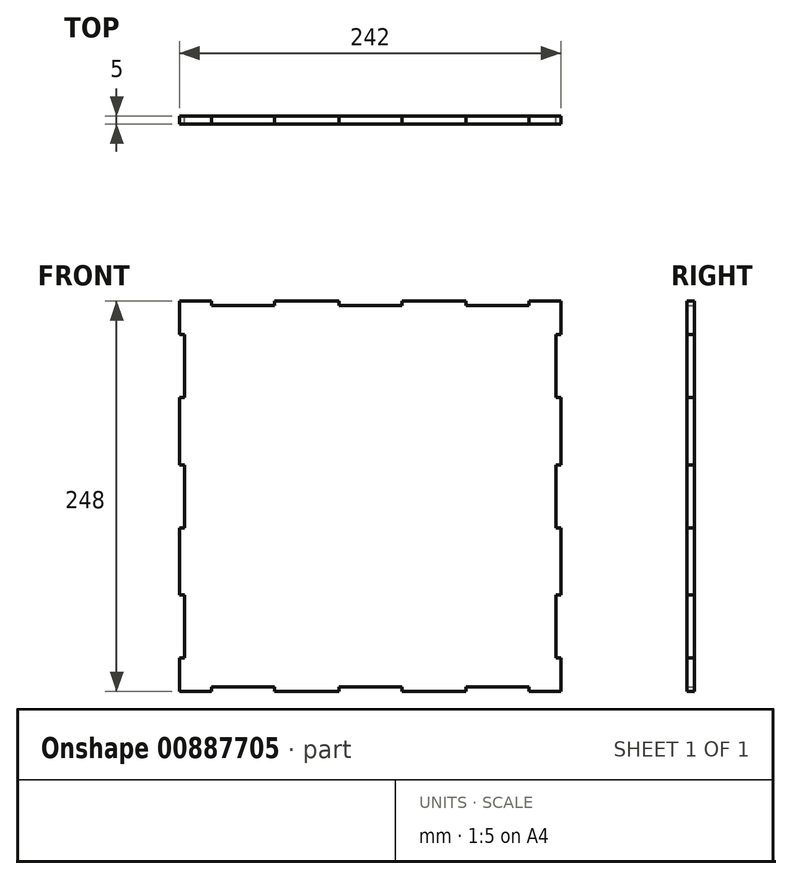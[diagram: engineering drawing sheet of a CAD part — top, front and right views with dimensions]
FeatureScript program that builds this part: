
annotation { "Feature Type Name" : "Feature", "Feature Type Description" : "" }
export const myFeature = defineFeature(function(context is Context, id is Id, definition is map)
    precondition{}
    {
        {
            var Q0;
            Q0=qCreatedBy(makeId("Front.planeOp"),FACE);
            var sketch = newSketch(context, id + "F0", { "sketchPlane" : qUnion([Q0])});
            skLineSegment(sketch, "E0.bottom", {"start": v(121, -124) * mm, "end": v(100.7, -124) * mm});
            skLineSegment(sketch, "E0.top", {"start": v(121, 124) * mm, "end": v(100.7, 124) * mm});
            skLineSegment(sketch, "E0.left", {"start": v(121, -124) * mm, "end": v(121, -102.67) * mm});
            skLineSegment(sketch, "E0.right", {"start": v(-121, -124) * mm, "end": v(-121, -102.67) * mm});
            skPoint(sketch, "E0.middle", {"position": v(0, 0) * mm});
            skLineSegment(sketch, "E1", {"start": v(-121, 102.67) * mm, "end": v(-118, 102.67) * mm});
            skLineSegment(sketch, "E2", {"start": v(-118, 102.67) * mm, "end": v(-118, 62.67) * mm});
            skLineSegment(sketch, "E3", {"start": v(-118, 62.67) * mm, "end": v(-121, 62.67) * mm});
            skLineSegment(sketch, "E4", {"start": v(-121, 20) * mm, "end": v(-118, 20) * mm});
            skLineSegment(sketch, "E5", {"start": v(-118, 20) * mm, "end": v(-118, -20) * mm});
            skLineSegment(sketch, "E6", {"start": v(-118, -20) * mm, "end": v(-121, -20) * mm});
            skLineSegment(sketch, "E7.MirrorCS", {"start": v(-118, -102.67) * mm, "end": v(-118, -62.67) * mm});
            skLineSegment(sketch, "E8.MirrorCS", {"start": v(-118, -62.67) * mm, "end": v(-121, -62.67) * mm});
            skLineSegment(sketch, "E9.MirrorCS", {"start": v(-121, -102.67) * mm, "end": v(-118, -102.67) * mm});
            skLineSegment(sketch, "E10.MirrorCS", {"start": v(118, 102.67) * mm, "end": v(118, 62.67) * mm});
            skLineSegment(sketch, "E11.MirrorCS", {"start": v(121, 102.67) * mm, "end": v(118, 102.67) * mm});
            skLineSegment(sketch, "E12.MirrorCS", {"start": v(118, 62.67) * mm, "end": v(121, 62.67) * mm});
            skLineSegment(sketch, "E13.MirrorCS", {"start": v(121, 20) * mm, "end": v(118, 20) * mm});
            skLineSegment(sketch, "E14.MirrorCS", {"start": v(118, 20) * mm, "end": v(118, -20) * mm});
            skLineSegment(sketch, "E15.MirrorCS", {"start": v(118, -20) * mm, "end": v(121, -20) * mm});
            skLineSegment(sketch, "E16.MirrorCS", {"start": v(118, -102.67) * mm, "end": v(118, -62.67) * mm});
            skLineSegment(sketch, "E17.MirrorCS", {"start": v(118, -62.67) * mm, "end": v(121, -62.67) * mm});
            skLineSegment(sketch, "E18.MirrorCS", {"start": v(121, -102.67) * mm, "end": v(118, -102.67) * mm});
            skLineSegment(sketch, "E19.trimOffspring", {"start": v(-121, 102.67) * mm, "end": v(-121, 124) * mm});
            skLineSegment(sketch, "E20.trimOffspring", {"start": v(-121, 20) * mm, "end": v(-121, 62.67) * mm});
            skLineSegment(sketch, "E21.trimOffspring", {"start": v(-121, -62.67) * mm, "end": v(-121, -20) * mm});
            skLineSegment(sketch, "E22.trimOffspring", {"start": v(121, 102.67) * mm, "end": v(121, 124) * mm});
            skLineSegment(sketch, "E23.trimOffspring", {"start": v(121, 20) * mm, "end": v(121, 62.67) * mm});
            skLineSegment(sketch, "E24.trimOffspring", {"start": v(121, -62.67) * mm, "end": v(121, -20) * mm});
            skLineSegment(sketch, "E25", {"start": v(100.7, -124) * mm, "end": v(100.7, -121) * mm});
            skLineSegment(sketch, "E26", {"start": v(100.7, -121) * mm, "end": v(60.7, -121) * mm});
            skLineSegment(sketch, "E27", {"start": v(60.7, -121) * mm, "end": v(60.7, -124) * mm});
            skLineSegment(sketch, "E28", {"start": v(20, -124) * mm, "end": v(20, -121) * mm});
            skLineSegment(sketch, "E29", {"start": v(20, -121) * mm, "end": v(-20, -121) * mm});
            skLineSegment(sketch, "E30", {"start": v(-20, -121) * mm, "end": v(-20, -124) * mm});
            skLineSegment(sketch, "E31.MirrorCS", {"start": v(-100.7, -124) * mm, "end": v(-100.7, -121) * mm});
            skLineSegment(sketch, "E32.MirrorCS", {"start": v(-100.7, -121) * mm, "end": v(-60.7, -121) * mm});
            skLineSegment(sketch, "E33.MirrorCS", {"start": v(-60.7, -121) * mm, "end": v(-60.7, -124) * mm});
            skLineSegment(sketch, "E34.trimOffspring", {"start": v(60.7, -124) * mm, "end": v(20, -124) * mm});
            skLineSegment(sketch, "E35.trimOffspring", {"start": v(-20, -124) * mm, "end": v(-60.7, -124) * mm});
            skLineSegment(sketch, "E36.trimOffspring", {"start": v(-100.7, -124) * mm, "end": v(-121, -124) * mm});
            skLineSegment(sketch, "E37.MirrorCS", {"start": v(100.7, 121) * mm, "end": v(60.7, 121) * mm});
            skLineSegment(sketch, "E38.MirrorCS", {"start": v(100.7, 124) * mm, "end": v(100.7, 121) * mm});
            skLineSegment(sketch, "E39.MirrorCS", {"start": v(60.7, 121) * mm, "end": v(60.7, 124) * mm});
            skLineSegment(sketch, "E40.MirrorCS", {"start": v(20, 124) * mm, "end": v(20, 121) * mm});
            skLineSegment(sketch, "E41.MirrorCS", {"start": v(20, 121) * mm, "end": v(-20, 121) * mm});
            skLineSegment(sketch, "E42.MirrorCS", {"start": v(-20, 121) * mm, "end": v(-20, 124) * mm});
            skLineSegment(sketch, "E43.MirrorCS", {"start": v(-60.7, 121) * mm, "end": v(-60.7, 124) * mm});
            skLineSegment(sketch, "E44.MirrorCS", {"start": v(-100.7, 121) * mm, "end": v(-60.7, 121) * mm});
            skLineSegment(sketch, "E45.MirrorCS", {"start": v(-100.7, 124) * mm, "end": v(-100.7, 121) * mm});
            skLineSegment(sketch, "E46.trimOffspring", {"start": v(-20, 124) * mm, "end": v(-60.7, 124) * mm});
            skLineSegment(sketch, "E47.trimOffspring", {"start": v(-100.7, 124) * mm, "end": v(-121, 124) * mm});
            skLineSegment(sketch, "E48.trimOffspring", {"start": v(60.7, 124) * mm, "end": v(20, 124) * mm});
            skSolve(sketch);
        }
        {
            var Q0;
            Q0 = qSketchRegion(id + "F0", true);
            var Q1;
            Q1=makeQuery(id+"F0.imprint","IMPRINT",FACE,{"disambiguationData":[TD([[makeQuery(id+"F0.imprint","IMPRINT",EDGE,{"derivedFrom":sQuery(id+"F0.wireOp",EDGE,"E0.bottom")}),-1.0]])]});
            extrude(context, id + "F1", {"entities" : qUnion([Q0, Q1]), "depth" : 5 * mm, "offsetDistance" : 25 * mm});
        }
    });
